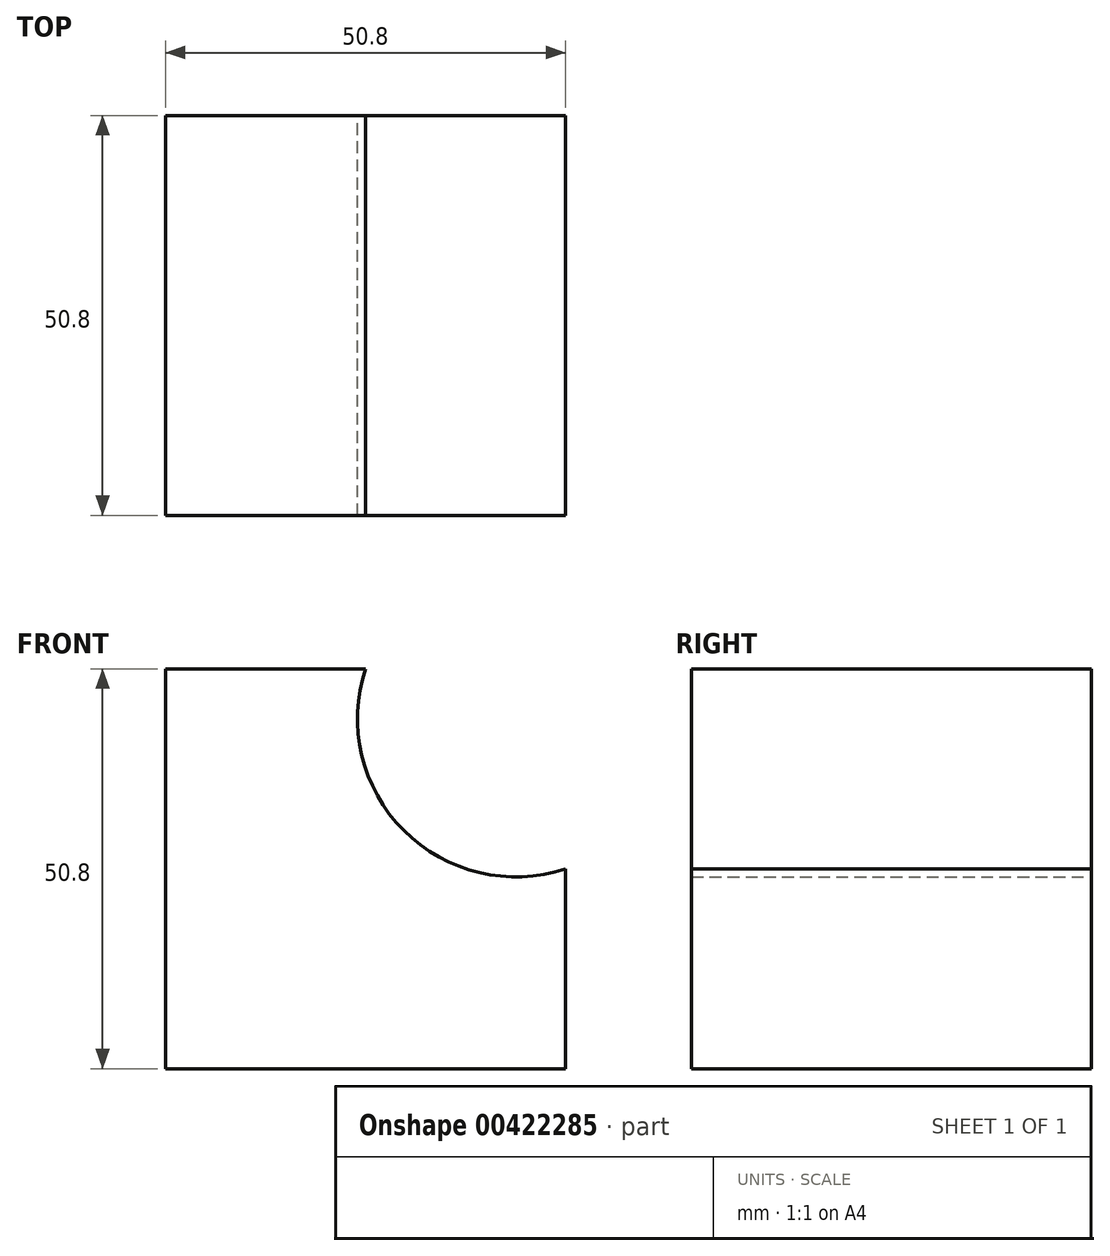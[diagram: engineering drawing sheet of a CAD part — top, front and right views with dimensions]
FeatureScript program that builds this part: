
annotation { "Feature Type Name" : "Feature", "Feature Type Description" : "" }
export const myFeature = defineFeature(function(context is Context, id is Id, definition is map)
    precondition{}
    {
        {
            var Q0;
            Q0=qCreatedBy(makeId("Front.planeOp"),FACE);
            var sketch = newSketch(context, id + "F0", { "sketchPlane" : qUnion([Q0])});
            skLineSegment(sketch, "E0", {"start": v(-55.03, 50.8) * mm, "end": v(-55.03, 0) * mm});
            skLineSegment(sketch, "E1", {"start": v(-55.03, 0) * mm, "end": v(-4.23, 0) * mm});
            skLineSegment(sketch, "E2", {"start": v(-4.23, 0) * mm, "end": v(-4.23, 25.4) * mm});
            skLineSegment(sketch, "E3", {"start": v(-55.03, 50.8) * mm, "end": v(-29.63, 50.8) * mm});
            skArc(sketch, "E4", {"start": v(-29.63, 50.8) * mm, "mid": v(-24.77, 30.26) * mm, "end": v(-4.23, 25.4) * mm});
            skSolve(sketch);
        }
        {
            var Q0;
            Q0 = qSketchRegion(id + "F0", true);
            extrude(context, id + "F1", {"entities" : qUnion([Q0]), "depth" : 50.8 * mm});
        }
    });
